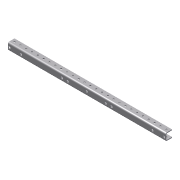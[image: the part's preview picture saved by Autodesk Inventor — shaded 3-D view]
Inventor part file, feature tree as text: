
AUTODESK INVENTOR PART (.ipt)
format: ipt  version: 2013 (Build 170138000, 138)  size: 230,400 bytes
history: native  units: in
note: dims shown in document units (in); Inventor stores cm internally (conversion verified against a paired STEP export)
features: projected_geometry x8, extrude x3, sketch x3, other x1, mirror x1, imported_body x1
ambient origin geometry x8: Origin, YZ Plane, XZ Plane, XY Plane, X Axis, Y Axis, Z Axis, Center Point
feature tree (17):
  other  "Short C Channel for drive1"
  extrude  "Extrusion1"  TaperAngle=0.0deg  [1 undecoded]
  extrude  "Extrusion2"  Depth=0.15in
  extrude  "Extrusion3"  Depth=1.0in TaperAngle=0.0deg
  mirror  "Mirror1"
  imported_body  "Base1"
  sketch  "Sketch1"  dims[d1=0.0in d3=0.0in]
  projected_geometry  "Projected Loop1"
  projected_geometry  "Projected Loop2"
  projected_geometry  "Projected Loop3"
  projected_geometry  "Projected Loop4"
  sketch  "Sketch2"  dims[d4=0.38in d5=0.15in]
  projected_geometry  "Projected Loop5"
  projected_geometry  "Projected Loop6"
  projected_geometry  "Projected Loop7"
  projected_geometry  "Projected Loop8"
  sketch  "Sketch3"  dims[d6=11.25in d7=1.0in d8=0.0in]
note: 1 required parameter value undecoded (feature->parameter linkage not recoverable at this tier; creation-order binding heuristic only, values carry confidence <= 0.55)
